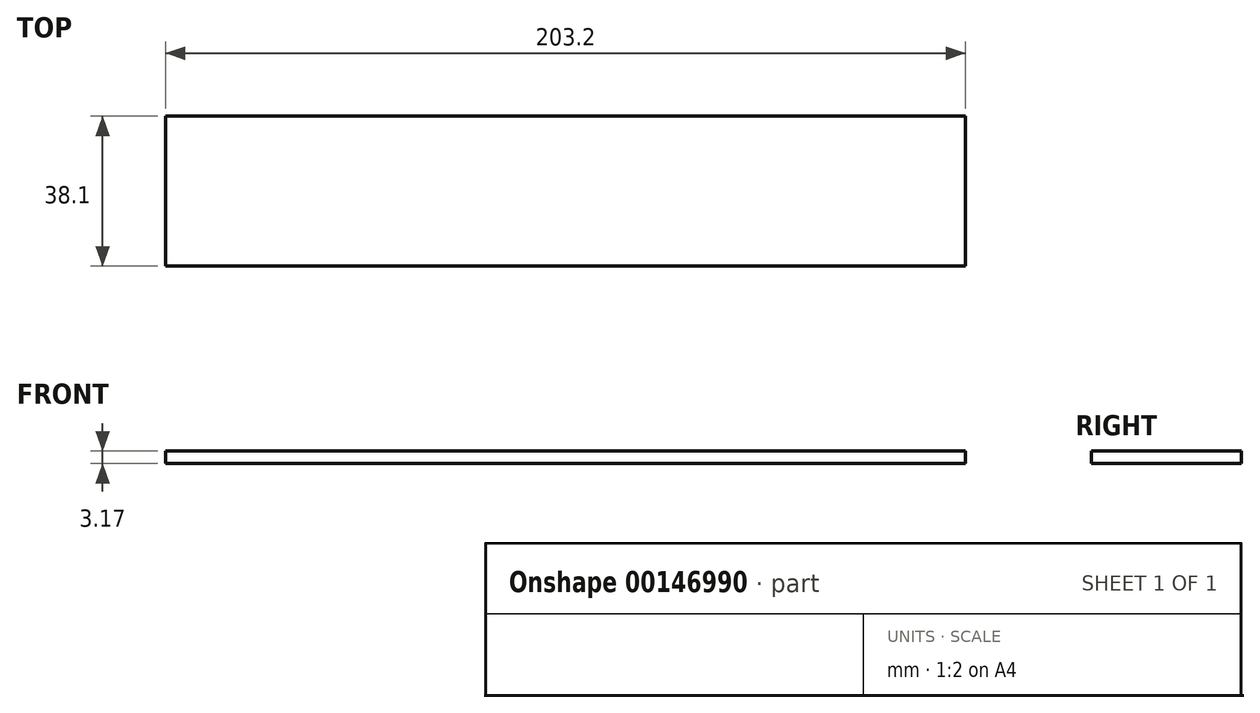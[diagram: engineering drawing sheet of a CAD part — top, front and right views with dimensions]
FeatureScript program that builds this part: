
annotation { "Feature Type Name" : "Feature", "Feature Type Description" : "" }
export const myFeature = defineFeature(function(context is Context, id is Id, definition is map)
    precondition{}
    {
        {
            var Q0;
            Q0=qCreatedBy(makeId("Top.planeOp"),FACE);
            var sketch = newSketch(context, id + "F0", { "sketchPlane" : qUnion([Q0])});
            skLineSegment(sketch, "E0.bottom", {"start": v(101.6, 19.05) * mm, "end": v(-101.6, 19.05) * mm});
            skLineSegment(sketch, "E0.top", {"start": v(101.6, -19.05) * mm, "end": v(-101.6, -19.05) * mm});
            skLineSegment(sketch, "E0.left", {"start": v(101.6, 19.05) * mm, "end": v(101.6, -19.05) * mm});
            skLineSegment(sketch, "E0.right", {"start": v(-101.6, 19.05) * mm, "end": v(-101.6, -19.05) * mm});
            skPoint(sketch, "E0.middle", {"position": v(0, 0) * mm});
            skSolve(sketch);
        }
        {
            var Q0;
            Q0 = qSketchRegion(id + "F0", true);
            extrude(context, id + "F1", {"entities" : qUnion([Q0]), "depth" : 3.17 * mm});
        }
    });
